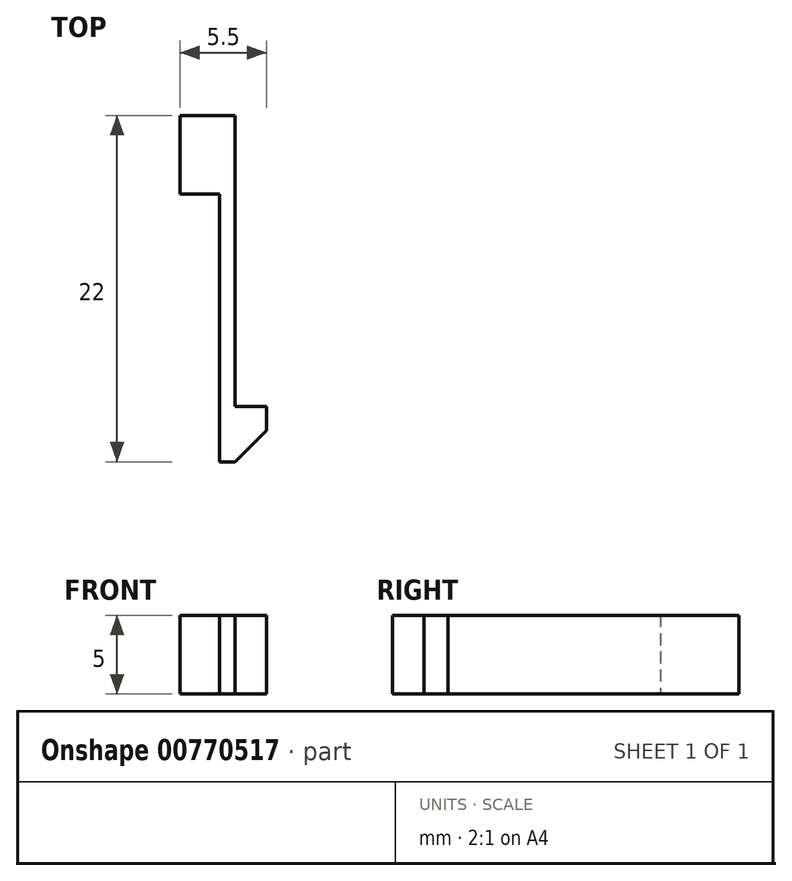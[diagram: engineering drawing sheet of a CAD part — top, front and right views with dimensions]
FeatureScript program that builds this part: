
annotation { "Feature Type Name" : "Feature", "Feature Type Description" : "" }
export const myFeature = defineFeature(function(context is Context, id is Id, definition is map)
    precondition{}
    {
        {
            var Q0;
            Q0=qCreatedBy(makeId("Top.planeOp"),FACE);
            var sketch = newSketch(context, id + "F0", { "sketchPlane" : qUnion([Q0])});
            skLineSegment(sketch, "E0", {"start": v(0, 17) * mm, "end": v(0, 0) * mm});
            skLineSegment(sketch, "E1", {"start": v(0, 0) * mm, "end": v(1, 0) * mm});
            skLineSegment(sketch, "E2", {"start": v(1, 0) * mm, "end": v(3, 2) * mm});
            skLineSegment(sketch, "E3", {"start": v(3, 2) * mm, "end": v(3, 3.5) * mm});
            skLineSegment(sketch, "E4", {"start": v(3, 3.5) * mm, "end": v(1, 3.5) * mm});
            skLineSegment(sketch, "E5", {"start": v(1, 3.5) * mm, "end": v(1, 22) * mm});
            skLineSegment(sketch, "E6", {"start": v(0, 17) * mm, "end": v(-2.5, 17) * mm});
            skLineSegment(sketch, "E7", {"start": v(-2.5, 17) * mm, "end": v(-2.5, 22) * mm});
            skLineSegment(sketch, "E8", {"start": v(-2.5, 22) * mm, "end": v(1, 22) * mm});
            skSolve(sketch);
        }
        {
            var Q0;
            Q0=qSketchRegion(id+"F0",true);
            extrude(context, id + "F1", {"entities" : qUnion([Q0]), "depth" : 5 * mm, "offsetDistance" : 25 * mm});
        }
    });
